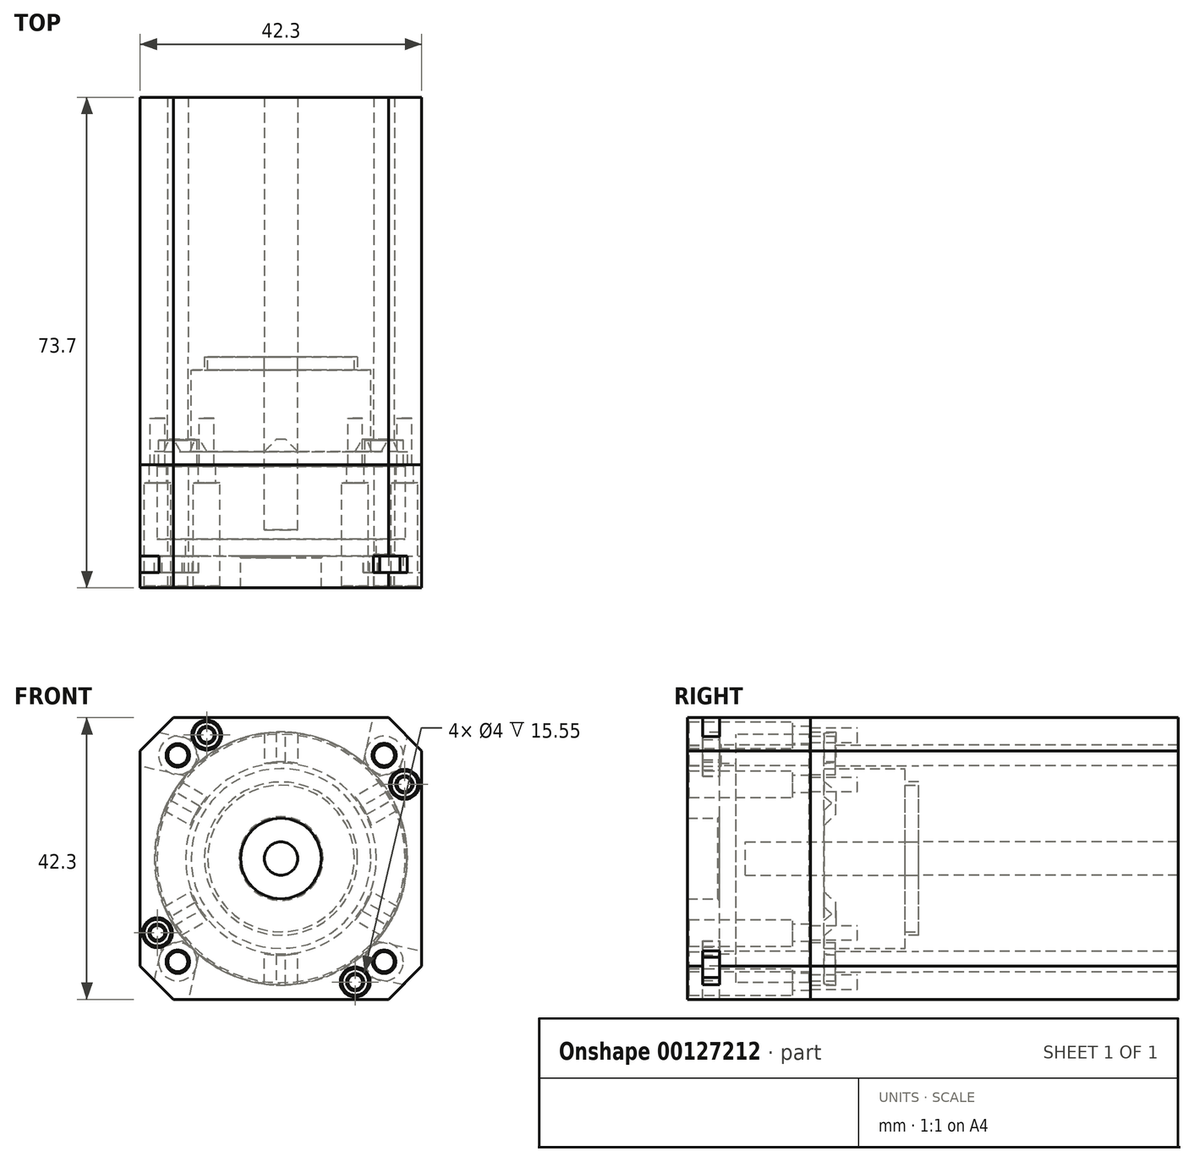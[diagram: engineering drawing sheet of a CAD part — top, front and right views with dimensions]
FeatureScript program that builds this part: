
annotation { "Feature Type Name" : "Feature", "Feature Type Description" : "" }
export const myFeature = defineFeature(function(context is Context, id is Id, definition is map)
    precondition{}
    {
        {
            var Q0;
            Q0=qCreatedBy(makeId("Front.planeOp"),FACE);
            var sketch = newSketch(context, id + "F0", { "sketchPlane" : qUnion([Q0])});
            skCircle(sketch, "E0", {"center": v(0, 0) * mm, "radius": 2.5 * mm});
            skLineSegment(sketch, "E1.bottom", {"start": v(21.15, -21.15) * mm, "end": v(-21.15, -21.15) * mm});
            skLineSegment(sketch, "E1.top", {"start": v(21.15, 21.15) * mm, "end": v(-21.15, 21.15) * mm});
            skLineSegment(sketch, "E1.left", {"start": v(21.15, -21.15) * mm, "end": v(21.15, 21.15) * mm});
            skLineSegment(sketch, "E1.right", {"start": v(-21.15, -21.15) * mm, "end": v(-21.15, 21.15) * mm});
            skCircle(sketch, "E2", {"center": v(0, 0) * mm, "radius": 11 * mm});
            skLineSegment(sketch, "E3", {"start": v(21.15, 21.15) * mm, "end": v(15.5, 21.15) * mm, "construction": true});
            skLineSegment(sketch, "E4", {"start": v(15.5, 21.15) * mm, "end": v(15.5, 15.5) * mm, "construction": true});
            skCircle(sketch, "E5", {"center": v(15.5, 15.5) * mm, "radius": 1.55 * mm});
            skCircle(sketch, "E6.1.0", {"center": v(-15.5, 15.5) * mm, "radius": 1.55 * mm});
            skCircle(sketch, "E6.2.0", {"center": v(-15.5, -15.5) * mm, "radius": 1.55 * mm});
            skCircle(sketch, "E6.3.0", {"center": v(15.5, -15.5) * mm, "radius": 1.55 * mm});
            skSolve(sketch);
        }
        {
            var Q0;
            Q0 = qSketchRegion(id + "F0", true);
            var Q1;
            Q1=makeQuery(id+"F0.imprint","IMPRINT",FACE,{"disambiguationData":[TD([[makeQuery(id+"F0.imprint","IMPRINT",EDGE,{"derivedFrom":sQuery(id+"F0.wireOp",EDGE,"E0")}),-1.0]])]});
            extrude(context, id + "F1", {"entities" : qUnion([Q0, Q1]), "oppositeDirection" : true, "depth" : 39 * mm});
        }
        {
            var Q0;
            Q0=makeQuery(id+"F0.imprint","IMPRINT",FACE,{"disambiguationData":[TD([[makeQuery(id+"F0.imprint","IMPRINT",EDGE,{"derivedFrom":sQuery(id+"F0.wireOp",EDGE,"E0")}),1.0]])]});
            extrude(context, id + "F2", {"entities" : qUnion([Q0]), "depth" : 26 * mm});
        }
        {
            var Q0;
            Q0=makeQuery(id+"F0.imprint","IMPRINT",FACE,{"disambiguationData":[TD([[makeQuery(id+"F0.imprint","IMPRINT",EDGE,{"derivedFrom":sQuery(id+"F0.wireOp",EDGE,"E0")}),-1.0]])]});
            extrude(context, id + "F3", {"entities" : qUnion([Q0]), "depth" : 2 * mm});
        }
        {
            var Q0;
            Q0=makeQuery(id+"F1.opExtrude","SWEPT_EDGE",EDGE,{"disambiguationData":[OSD([sQuery(id+"F0.wireOp",EDGE,"E1.top"),sQuery(id+"F0.wireOp",EDGE,"E1.left")])]});
            var Q1;
            Q1=makeQuery(id+"F1.opExtrude","SWEPT_EDGE",EDGE,{"disambiguationData":[OSD([sQuery(id+"F0.wireOp",EDGE,"E1.bottom"),sQuery(id+"F0.wireOp",EDGE,"E1.left")])]});
            var Q2;
            Q2=makeQuery(id+"F1.opExtrude","SWEPT_EDGE",EDGE,{"disambiguationData":[OSD([sQuery(id+"F0.wireOp",EDGE,"E1.bottom"),sQuery(id+"F0.wireOp",EDGE,"E1.right")])]});
            var Q3;
            Q3=makeQuery(id+"F1.opExtrude","SWEPT_EDGE",EDGE,{"disambiguationData":[OSD([sQuery(id+"F0.wireOp",EDGE,"E1.top"),sQuery(id+"F0.wireOp",EDGE,"E1.right")])]});
            chamfer(context, id + "F4", {"entities" : qUnion([Q0, Q1, Q2, Q3]), "width" : 5 * mm, "tangentPropagation" : true});
        }
        {
            var Q0;
            Q0=qCreatedBy(makeId("Front.planeOp"),FACE);
            cPlane(context, id + "F5", {"entities" : qUnion([Q0]), "cplaneType" : CPlaneType.OFFSET, "offset" : 2 * mm, "width" : 150 * mm, "height" : 150 * mm});
        }
        {
            var Q0;
            Q0=qCreatedBy(id+"F5.planeOp",FACE);
            var sketch = newSketch(context, id + "F6", { "sketchPlane" : qUnion([Q0])});
            skCircle(sketch, "E7", {"center": v(0, 0) * mm, "radius": 2.5 * mm});
            skLineSegment(sketch, "E8.bottom", {"start": v(21.15, -21.15) * mm, "end": v(-21.15, -21.15) * mm});
            skLineSegment(sketch, "E8.top", {"start": v(21.15, 21.15) * mm, "end": v(-21.15, 21.15) * mm});
            skLineSegment(sketch, "E8.left", {"start": v(21.15, -21.15) * mm, "end": v(21.15, 21.15) * mm});
            skLineSegment(sketch, "E8.right", {"start": v(-21.15, -21.15) * mm, "end": v(-21.15, 21.15) * mm});
            skCircle(sketch, "E9", {"center": v(0, 0) * mm, "radius": 11.5 * mm});
            skLineSegment(sketch, "E10", {"start": v(21.15, 21.15) * mm, "end": v(15.5, 21.15) * mm, "construction": true});
            skLineSegment(sketch, "E11", {"start": v(15.5, 21.15) * mm, "end": v(15.5, 15.5) * mm, "construction": true});
            skCircle(sketch, "E12", {"center": v(15.5, 15.5) * mm, "radius": 1.55 * mm});
            skCircle(sketch, "E13.1.0", {"center": v(-15.5, 15.5) * mm, "radius": 1.55 * mm});
            skCircle(sketch, "E13.2.0", {"center": v(-15.5, -15.5) * mm, "radius": 1.55 * mm});
            skCircle(sketch, "E13.3.0", {"center": v(15.5, -15.5) * mm, "radius": 1.55 * mm});
            skCircle(sketch, "E14", {"center": v(0, 0) * mm, "radius": 13.5 * mm});
            skSolve(sketch);
        }
        {
            var Q0;
            Q0=makeQuery(id+"F6.imprint","IMPRINT",FACE,{"disambiguationData":[TD([[makeQuery(id+"F6.imprint","IMPRINT",EDGE,{"derivedFrom":sQuery(id+"F6.wireOp",EDGE,"E8.bottom")}),-1.0]])]});
            extrude(context, id + "F7", {"entities" : qUnion([Q0]), "operationType" : NewBodyOperationType.ADD, "depth" : 12.2 * mm});
        }
        {
            var Q0;
            Q0=makeQuery(id+"F6.imprint","IMPRINT",FACE,{"disambiguationData":[TD([[makeQuery(id+"F6.imprint","IMPRINT",EDGE,{"derivedFrom":sQuery(id+"F6.wireOp",EDGE,"E9")}),-1.0]])]});
            var Q1;
            Q1=makeQuery(id+"F6.imprint","IMPRINT",FACE,{"disambiguationData":[TD([[makeQuery(id+"F6.imprint","IMPRINT",EDGE,{"derivedFrom":sQuery(id+"F6.wireOp",EDGE,"E8.bottom")}),-1.0]])]});
            extrude(context, id + "F8", {"entities" : qUnion([Q0, Q1]), "operationType" : NewBodyOperationType.ADD, "oppositeDirection" : true, "depth" : 2 * mm});
        }
        {
            var Q0;
            Q0=qCreatedBy(id+"F5.planeOp",FACE);
            cPlane(context, id + "F9", {"entities" : qUnion([Q0]), "cplaneType" : CPlaneType.OFFSET, "offset" : 12.2 * mm, "width" : 150 * mm, "height" : 150 * mm});
        }
        {
            var Q0;
            Q0=qCreatedBy(id+"F9.planeOp",FACE);
            var sketch = newSketch(context, id + "F10", { "sketchPlane" : qUnion([Q0])});
            skCircle(sketch, "E15", {"center": v(0, 0) * mm, "radius": 2.5 * mm});
            skLineSegment(sketch, "E16.bottom", {"start": v(21.15, -21.15) * mm, "end": v(-21.15, -21.15) * mm});
            skLineSegment(sketch, "E16.top", {"start": v(21.15, 21.15) * mm, "end": v(-21.15, 21.15) * mm});
            skLineSegment(sketch, "E16.left", {"start": v(21.15, -21.15) * mm, "end": v(21.15, 21.15) * mm});
            skLineSegment(sketch, "E16.right", {"start": v(-21.15, -21.15) * mm, "end": v(-21.15, 21.15) * mm});
            skCircle(sketch, "E17", {"center": v(0, 0) * mm, "radius": 11.5 * mm});
            skLineSegment(sketch, "E18", {"start": v(21.15, 21.15) * mm, "end": v(15.5, 21.15) * mm, "construction": true});
            skLineSegment(sketch, "E19", {"start": v(15.5, 21.15) * mm, "end": v(15.5, 15.5) * mm, "construction": true});
            skCircle(sketch, "E20", {"center": v(15.5, 15.5) * mm, "radius": 1.55 * mm});
            skCircle(sketch, "E21.1.0", {"center": v(-15.5, 15.5) * mm, "radius": 1.55 * mm});
            skCircle(sketch, "E21.2.0", {"center": v(-15.5, -15.5) * mm, "radius": 1.55 * mm});
            skCircle(sketch, "E21.3.0", {"center": v(15.5, -15.5) * mm, "radius": 1.55 * mm});
            skCircle(sketch, "E22", {"center": v(0, 0) * mm, "radius": 13.5 * mm});
            skCircle(sketch, "E23", {"center": v(0, 0) * mm, "radius": 19 * mm});
            skCircle(sketch, "E24", {"center": v(0, 0) * mm, "radius": 14.5 * mm});
            skLineSegment(sketch, "E25", {"start": v(2.5, 18.83) * mm, "end": v(2.5, 14.28) * mm});
            skLineSegment(sketch, "E26", {"start": v(-2.5, 18.83) * mm, "end": v(-2.5, 14.28) * mm});
            skCircle(sketch, "E27", {"center": v(18.55, 11.15) * mm, "radius": 1.1 * mm});
            skCircle(sketch, "E28.1.0", {"center": v(-11.15, 18.55) * mm, "radius": 1.1 * mm});
            skCircle(sketch, "E28.2.0", {"center": v(-18.55, -11.15) * mm, "radius": 1.1 * mm});
            skCircle(sketch, "E28.3.0", {"center": v(11.15, -18.55) * mm, "radius": 1.1 * mm});
            skCircle(sketch, "E29", {"center": v(-15.5, 15.5) * mm, "radius": 2.88 * mm});
            skCircle(sketch, "E30.1.0", {"center": v(-15.5, -15.5) * mm, "radius": 2.88 * mm});
            skCircle(sketch, "E30.2.0", {"center": v(15.5, -15.5) * mm, "radius": 2.88 * mm});
            skCircle(sketch, "E30.3.0", {"center": v(15.5, 15.5) * mm, "radius": 2.88 * mm});
            skLineSegment(sketch, "E31", {"start": v(0, 0) * mm, "end": v(0, 19) * mm, "construction": true});
            skLineSegment(sketch, "E32.1.0", {"start": v(-17.56, 7.25) * mm, "end": v(-13.62, 4.98) * mm});
            skLineSegment(sketch, "E32.1.1", {"start": v(-15.06, 11.58) * mm, "end": v(-11.12, 9.3) * mm});
            skLineSegment(sketch, "E32.2.0", {"start": v(-15.06, -11.58) * mm, "end": v(-11.12, -9.3) * mm});
            skLineSegment(sketch, "E32.2.1", {"start": v(-17.56, -7.25) * mm, "end": v(-13.62, -4.98) * mm});
            skLineSegment(sketch, "E32.3.0", {"start": v(2.5, -18.83) * mm, "end": v(2.5, -14.28) * mm});
            skLineSegment(sketch, "E32.3.1", {"start": v(-2.5, -18.83) * mm, "end": v(-2.5, -14.28) * mm});
            skLineSegment(sketch, "E32.4.0", {"start": v(17.56, -7.25) * mm, "end": v(13.62, -4.98) * mm});
            skLineSegment(sketch, "E32.4.1", {"start": v(15.06, -11.58) * mm, "end": v(11.12, -9.3) * mm});
            skLineSegment(sketch, "E32.5.0", {"start": v(15.06, 11.58) * mm, "end": v(11.12, 9.3) * mm});
            skLineSegment(sketch, "E32.5.1", {"start": v(17.56, 7.25) * mm, "end": v(13.62, 4.98) * mm});
            skSolve(sketch);
        }
        {
            var Q0;
            Q0=makeQuery(id+"F10.imprint","IMPRINT",FACE,{"disambiguationData":[TD([[makeQuery(id+"F10.imprint","IMPRINT",EDGE,{"derivedFrom":sQuery(id+"F10.wireOp",EDGE,"E16.bottom")}),-1.0]])]});
            extrude(context, id + "F11", {"entities" : qUnion([Q0]), "operationType" : NewBodyOperationType.ADD, "depth" : 2 * mm});
        }
        {
            var Q0;
            Q0=makeQuery(id+"F11.boolean.opBoolean","SPLIT",FACE,{"disambiguationData":[TD([makeQuery(id+"F11.opExtrude","SWEPT_FACE",FACE,{"disambiguationData":[OSD([sQuery(id+"F10.wireOp",EDGE,"E28.1.0")])]})])],"derivedFrom":makeQuery(id+"F7.opExtrude","CAP_FACE",FACE,{"disambiguationData":[OSD([sQuery(id+"F6.wireOp",EDGE,"E8.bottom"),sQuery(id+"F6.wireOp",EDGE,"E8.top"),sQuery(id+"F6.wireOp",EDGE,"E8.left"),sQuery(id+"F6.wireOp",EDGE,"E8.right"),sQuery(id+"F6.wireOp",EDGE,"E12"),sQuery(id+"F6.wireOp",EDGE,"E13.1.0"),sQuery(id+"F6.wireOp",EDGE,"E13.2.0"),sQuery(id+"F6.wireOp",EDGE,"E13.3.0"),sQuery(id+"F6.wireOp",EDGE,"E14")])],"isStart":false})});
            var Q1;
            Q1=makeQuery(id+"F11.boolean.opBoolean","SPLIT",FACE,{"disambiguationData":[TD([makeQuery(id+"F11.opExtrude","SWEPT_FACE",FACE,{"disambiguationData":[OSD([sQuery(id+"F10.wireOp",EDGE,"E27")])]})])],"derivedFrom":makeQuery(id+"F7.opExtrude","CAP_FACE",FACE,{"disambiguationData":[OSD([sQuery(id+"F6.wireOp",EDGE,"E8.bottom"),sQuery(id+"F6.wireOp",EDGE,"E8.top"),sQuery(id+"F6.wireOp",EDGE,"E8.left"),sQuery(id+"F6.wireOp",EDGE,"E8.right"),sQuery(id+"F6.wireOp",EDGE,"E12"),sQuery(id+"F6.wireOp",EDGE,"E13.1.0"),sQuery(id+"F6.wireOp",EDGE,"E13.2.0"),sQuery(id+"F6.wireOp",EDGE,"E13.3.0"),sQuery(id+"F6.wireOp",EDGE,"E14")])],"isStart":false})});
            var Q2;
            Q2=makeQuery(id+"F11.boolean.opBoolean","SPLIT",FACE,{"disambiguationData":[TD([makeQuery(id+"F11.opExtrude","SWEPT_FACE",FACE,{"disambiguationData":[OSD([sQuery(id+"F10.wireOp",EDGE,"E28.2.0")])]})])],"derivedFrom":makeQuery(id+"F7.opExtrude","CAP_FACE",FACE,{"disambiguationData":[OSD([sQuery(id+"F6.wireOp",EDGE,"E8.bottom"),sQuery(id+"F6.wireOp",EDGE,"E8.top"),sQuery(id+"F6.wireOp",EDGE,"E8.left"),sQuery(id+"F6.wireOp",EDGE,"E8.right"),sQuery(id+"F6.wireOp",EDGE,"E12"),sQuery(id+"F6.wireOp",EDGE,"E13.1.0"),sQuery(id+"F6.wireOp",EDGE,"E13.2.0"),sQuery(id+"F6.wireOp",EDGE,"E13.3.0"),sQuery(id+"F6.wireOp",EDGE,"E14")])],"isStart":false})});
            var Q3;
            Q3=makeQuery(id+"F11.boolean.opBoolean","SPLIT",FACE,{"disambiguationData":[TD([makeQuery(id+"F11.opExtrude","SWEPT_FACE",FACE,{"disambiguationData":[OSD([sQuery(id+"F10.wireOp",EDGE,"E28.3.0")])]})])],"derivedFrom":makeQuery(id+"F7.opExtrude","CAP_FACE",FACE,{"disambiguationData":[OSD([sQuery(id+"F6.wireOp",EDGE,"E8.bottom"),sQuery(id+"F6.wireOp",EDGE,"E8.top"),sQuery(id+"F6.wireOp",EDGE,"E8.left"),sQuery(id+"F6.wireOp",EDGE,"E8.right"),sQuery(id+"F6.wireOp",EDGE,"E12"),sQuery(id+"F6.wireOp",EDGE,"E13.1.0"),sQuery(id+"F6.wireOp",EDGE,"E13.2.0"),sQuery(id+"F6.wireOp",EDGE,"E13.3.0"),sQuery(id+"F6.wireOp",EDGE,"E14")])],"isStart":false})});
            extrude(context, id + "F12", {"entities" : qUnion([Q0, Q1, Q2, Q3]), "operationType" : NewBodyOperationType.REMOVE, "oppositeDirection" : true, "depth" : 5 * mm});
        }
        {
            var Q0;
            {var subQ0=sQuery(id+"F10.wireOp",EDGE,"E25");Q0=makeQuery(id+"F10.imprint","IMPRINT",FACE,{"disambiguationData":[TD([[makeQuery(id+"F10.imprint","IMPRINT",EDGE,{"derivedFrom":subQ0}),-1.0]])]});}
            var Q1;
            {var subQ0=sQuery(id+"F10.wireOp",EDGE,"E32.5.0");Q1=makeQuery(id+"F10.imprint","IMPRINT",FACE,{"disambiguationData":[TD([[makeQuery(id+"F10.imprint","IMPRINT",EDGE,{"derivedFrom":subQ0}),1.0]])]});}
            var Q2;
            {var subQ0=sQuery(id+"F10.wireOp",EDGE,"E32.4.0");Q2=makeQuery(id+"F10.imprint","IMPRINT",FACE,{"disambiguationData":[TD([[makeQuery(id+"F10.imprint","IMPRINT",EDGE,{"derivedFrom":subQ0}),1.0]])]});}
            var Q3;
            {var subQ0=sQuery(id+"F10.wireOp",EDGE,"E32.3.0");Q3=makeQuery(id+"F10.imprint","IMPRINT",FACE,{"disambiguationData":[TD([[makeQuery(id+"F10.imprint","IMPRINT",EDGE,{"derivedFrom":subQ0}),1.0]])]});}
            var Q4;
            {var subQ0=sQuery(id+"F10.wireOp",EDGE,"E32.2.0");Q4=makeQuery(id+"F10.imprint","IMPRINT",FACE,{"disambiguationData":[TD([[makeQuery(id+"F10.imprint","IMPRINT",EDGE,{"derivedFrom":subQ0}),1.0]])]});}
            var Q5;
            {var subQ0=sQuery(id+"F10.wireOp",EDGE,"E32.1.0");Q5=makeQuery(id+"F10.imprint","IMPRINT",FACE,{"disambiguationData":[TD([[makeQuery(id+"F10.imprint","IMPRINT",EDGE,{"derivedFrom":subQ0}),1.0]])]});}
            extrude(context, id + "F13", {"entities" : qUnion([Q0, Q1, Q2, Q3, Q4, Q5]), "operationType" : NewBodyOperationType.REMOVE, "oppositeDirection" : true, "depth" : 1.8 * mm});
        }
        {
            var Q0;
            {var subQ0=sQuery(id+"F6.wireOp",EDGE,"E13.1.0");Q0=makeQuery(id+"F11.boolean.opBoolean","SPLIT",FACE,{"disambiguationData":[TD([makeQuery(id+"F7.opExtrude","SWEPT_FACE",FACE,{"disambiguationData":[OSD([subQ0])]})])],"derivedFrom":makeQuery(id+"F7.opExtrude","CAP_FACE",FACE,{"disambiguationData":[OSD([sQuery(id+"F6.wireOp",EDGE,"E8.bottom"),sQuery(id+"F6.wireOp",EDGE,"E8.top"),sQuery(id+"F6.wireOp",EDGE,"E8.left"),sQuery(id+"F6.wireOp",EDGE,"E8.right"),sQuery(id+"F6.wireOp",EDGE,"E12"),subQ0,sQuery(id+"F6.wireOp",EDGE,"E13.2.0"),sQuery(id+"F6.wireOp",EDGE,"E13.3.0"),sQuery(id+"F6.wireOp",EDGE,"E14")])],"isStart":false})});}
            var Q1;
            {var subQ0=sQuery(id+"F6.wireOp",EDGE,"E13.2.0");Q1=makeQuery(id+"F11.boolean.opBoolean","SPLIT",FACE,{"disambiguationData":[TD([makeQuery(id+"F7.opExtrude","SWEPT_FACE",FACE,{"disambiguationData":[OSD([subQ0])]})])],"derivedFrom":makeQuery(id+"F7.opExtrude","CAP_FACE",FACE,{"disambiguationData":[OSD([sQuery(id+"F6.wireOp",EDGE,"E8.bottom"),sQuery(id+"F6.wireOp",EDGE,"E8.top"),sQuery(id+"F6.wireOp",EDGE,"E8.left"),sQuery(id+"F6.wireOp",EDGE,"E8.right"),sQuery(id+"F6.wireOp",EDGE,"E12"),sQuery(id+"F6.wireOp",EDGE,"E13.1.0"),subQ0,sQuery(id+"F6.wireOp",EDGE,"E13.3.0"),sQuery(id+"F6.wireOp",EDGE,"E14")])],"isStart":false})});}
            var Q2;
            {var subQ0=sQuery(id+"F6.wireOp",EDGE,"E13.3.0");Q2=makeQuery(id+"F11.boolean.opBoolean","SPLIT",FACE,{"disambiguationData":[TD([makeQuery(id+"F7.opExtrude","SWEPT_FACE",FACE,{"disambiguationData":[OSD([subQ0])]})])],"derivedFrom":makeQuery(id+"F7.opExtrude","CAP_FACE",FACE,{"disambiguationData":[OSD([sQuery(id+"F6.wireOp",EDGE,"E8.bottom"),sQuery(id+"F6.wireOp",EDGE,"E8.top"),sQuery(id+"F6.wireOp",EDGE,"E8.left"),sQuery(id+"F6.wireOp",EDGE,"E8.right"),sQuery(id+"F6.wireOp",EDGE,"E12"),sQuery(id+"F6.wireOp",EDGE,"E13.1.0"),sQuery(id+"F6.wireOp",EDGE,"E13.2.0"),subQ0,sQuery(id+"F6.wireOp",EDGE,"E14")])],"isStart":false})});}
            var Q3;
            {var subQ0=sQuery(id+"F6.wireOp",EDGE,"E12");Q3=makeQuery(id+"F11.boolean.opBoolean","SPLIT",FACE,{"disambiguationData":[TD([makeQuery(id+"F7.opExtrude","SWEPT_FACE",FACE,{"disambiguationData":[OSD([subQ0])]})])],"derivedFrom":makeQuery(id+"F7.opExtrude","CAP_FACE",FACE,{"disambiguationData":[OSD([sQuery(id+"F6.wireOp",EDGE,"E8.bottom"),sQuery(id+"F6.wireOp",EDGE,"E8.top"),sQuery(id+"F6.wireOp",EDGE,"E8.left"),sQuery(id+"F6.wireOp",EDGE,"E8.right"),subQ0,sQuery(id+"F6.wireOp",EDGE,"E13.1.0"),sQuery(id+"F6.wireOp",EDGE,"E13.2.0"),sQuery(id+"F6.wireOp",EDGE,"E13.3.0"),sQuery(id+"F6.wireOp",EDGE,"E14")])],"isStart":false})});}
            extrude(context, id + "F14", {"entities" : qUnion([Q0, Q1, Q2, Q3]), "operationType" : NewBodyOperationType.REMOVE, "oppositeDirection" : true, "depth" : 1.7 * mm});
        }
        {
            var Q0;
            Q0=makeQuery(id+"F13.boolean.opBoolean","COPY",EDGE,{"derivedFrom":makeQuery(id+"F13.opExtrude","CAP_EDGE",EDGE,{"disambiguationData":[OSD([sQuery(id+"F10.wireOp",EDGE,"E26")])],"isStart":false})});
            var Q1;
            Q1=makeQuery(id+"F13.boolean.opBoolean","COPY",EDGE,{"derivedFrom":makeQuery(id+"F13.opExtrude","CAP_EDGE",EDGE,{"disambiguationData":[OSD([sQuery(id+"F10.wireOp",EDGE,"E32.1.1")])],"isStart":false})});
            var Q2;
            Q2=makeQuery(id+"F13.boolean.opBoolean","COPY",EDGE,{"derivedFrom":makeQuery(id+"F13.opExtrude","CAP_EDGE",EDGE,{"disambiguationData":[OSD([sQuery(id+"F10.wireOp",EDGE,"E32.5.0")])],"isStart":false})});
            var Q3;
            Q3=makeQuery(id+"F13.boolean.opBoolean","COPY",EDGE,{"derivedFrom":makeQuery(id+"F13.opExtrude","CAP_EDGE",EDGE,{"disambiguationData":[OSD([sQuery(id+"F10.wireOp",EDGE,"E32.2.1")])],"isStart":false})});
            var Q4;
            Q4=makeQuery(id+"F13.boolean.opBoolean","COPY",EDGE,{"derivedFrom":makeQuery(id+"F13.opExtrude","CAP_EDGE",EDGE,{"disambiguationData":[OSD([sQuery(id+"F10.wireOp",EDGE,"E32.3.1")])],"isStart":false})});
            var Q5;
            Q5=makeQuery(id+"F13.boolean.opBoolean","COPY",EDGE,{"derivedFrom":makeQuery(id+"F13.opExtrude","CAP_EDGE",EDGE,{"disambiguationData":[OSD([sQuery(id+"F10.wireOp",EDGE,"E32.4.0")])],"isStart":false})});
            var Q6;
            Q6=makeQuery(id+"F13.boolean.opBoolean","COPY",EDGE,{"derivedFrom":makeQuery(id+"F13.opExtrude","CAP_EDGE",EDGE,{"disambiguationData":[OSD([sQuery(id+"F10.wireOp",EDGE,"E25")])],"isStart":false})});
            var Q7;
            Q7=makeQuery(id+"F13.boolean.opBoolean","COPY",EDGE,{"derivedFrom":makeQuery(id+"F13.opExtrude","CAP_EDGE",EDGE,{"disambiguationData":[OSD([sQuery(id+"F10.wireOp",EDGE,"E32.5.1")])],"isStart":false})});
            var Q8;
            Q8=makeQuery(id+"F13.boolean.opBoolean","COPY",EDGE,{"derivedFrom":makeQuery(id+"F13.opExtrude","CAP_EDGE",EDGE,{"disambiguationData":[OSD([sQuery(id+"F10.wireOp",EDGE,"E32.3.0")])],"isStart":false})});
            var Q9;
            Q9=makeQuery(id+"F13.boolean.opBoolean","COPY",EDGE,{"derivedFrom":makeQuery(id+"F13.opExtrude","CAP_EDGE",EDGE,{"disambiguationData":[OSD([sQuery(id+"F10.wireOp",EDGE,"E32.2.0")])],"isStart":false})});
            var Q10;
            Q10=makeQuery(id+"F13.boolean.opBoolean","COPY",EDGE,{"derivedFrom":makeQuery(id+"F13.opExtrude","CAP_EDGE",EDGE,{"disambiguationData":[OSD([sQuery(id+"F10.wireOp",EDGE,"E32.1.0")])],"isStart":false})});
            var Q11;
            Q11=makeQuery(id+"F13.boolean.opBoolean","COPY",EDGE,{"derivedFrom":makeQuery(id+"F13.opExtrude","CAP_EDGE",EDGE,{"disambiguationData":[OSD([sQuery(id+"F10.wireOp",EDGE,"E32.4.1")])],"isStart":false})});
            chamfer(context, id + "F15", {"entities" : qUnion([Q0, Q1, Q2, Q3, Q4, Q5, Q6, Q7, Q8, Q9, Q10, Q11]), "width" : 1.8 * mm, "tangentPropagation" : true});
        }
        {
            var Q0;
            Q0=qCreatedBy(id+"F9.planeOp",FACE);
            cPlane(context, id + "F16", {"entities" : qUnion([Q0]), "cplaneType" : CPlaneType.OFFSET, "offset" : 13.2 * mm, "width" : 150 * mm, "height" : 150 * mm});
        }
        {
            var Q0;
            Q0=qCreatedBy(id+"F16.planeOp",FACE);
            var sketch = newSketch(context, id + "F17", { "sketchPlane" : qUnion([Q0])});
            skLineSegment(sketch, "E33.bottom", {"start": v(21.15, -21.15) * mm, "end": v(-21.15, -21.15) * mm});
            skLineSegment(sketch, "E33.top", {"start": v(21.15, 21.15) * mm, "end": v(-21.15, 21.15) * mm});
            skLineSegment(sketch, "E33.left", {"start": v(21.15, -21.15) * mm, "end": v(21.15, 21.15) * mm});
            skLineSegment(sketch, "E33.right", {"start": v(-21.15, -21.15) * mm, "end": v(-21.15, 21.15) * mm});
            skPoint(sketch, "E33.middle", {"position": v(0, 0) * mm});
            skLineSegment(sketch, "E34", {"start": v(21.15, 21.15) * mm, "end": v(15.5, 21.15) * mm, "construction": true});
            skLineSegment(sketch, "E35", {"start": v(15.5, 21.15) * mm, "end": v(15.5, 15.5) * mm, "construction": true});
            skCircle(sketch, "E36", {"center": v(15.5, 15.5) * mm, "radius": 1.55 * mm});
            skCircle(sketch, "E37.1.0", {"center": v(-15.5, 15.5) * mm, "radius": 1.55 * mm});
            skCircle(sketch, "E37.2.0", {"center": v(-15.5, -15.5) * mm, "radius": 1.55 * mm});
            skCircle(sketch, "E37.3.0", {"center": v(15.5, -15.5) * mm, "radius": 1.55 * mm});
            skCircle(sketch, "E38", {"center": v(0, 0) * mm, "radius": 18.65 * mm});
            skPoint(sketch, "E39.center", {"position": v(-0.77, 0.3) * mm});
            skLineSegment(sketch, "E39.anchor1", {"start": v(-0.77, 0.3) * mm, "end": v(-2.75, 12.92) * mm, "construction": true});
            skLineSegment(sketch, "E39.anchor2", {"start": v(-0.77, 0.3) * mm, "end": v(-13.7, 5.28) * mm, "construction": true});
            skCircle(sketch, "E40", {"center": v(0, 0) * mm, "radius": 6.2 * mm});
            skCircle(sketch, "E41", {"center": v(0, 0) * mm, "radius": 14.32 * mm});
            skSolve(sketch);
        }
        {
            var Q0;
            Q0=makeQuery(id+"F17.imprint","IMPRINT",FACE,{"disambiguationData":[TD([[makeQuery(id+"F17.imprint","IMPRINT",EDGE,{"derivedFrom":sQuery(id+"F17.wireOp",EDGE,"E33.bottom")}),-1.0]])]});
            extrude(context, id + "F18", {"entities" : qUnion([Q0]), "oppositeDirection" : true, "depth" : 11.2 * mm});
        }
        {
            var Q0;
            Q0=makeQuery(id+"F17.imprint","IMPRINT",FACE,{"disambiguationData":[TD([[makeQuery(id+"F17.imprint","IMPRINT",EDGE,{"derivedFrom":sQuery(id+"F17.wireOp",EDGE,"E33.bottom")}),-1.0]])]});
            var Q1;
            Q1=makeQuery(id+"F17.imprint","IMPRINT",FACE,{"disambiguationData":[TD([[makeQuery(id+"F17.imprint","IMPRINT",EDGE,{"derivedFrom":sQuery(id+"F17.wireOp",EDGE,"E38")}),1.0]])]});
            extrude(context, id + "F19", {"entities" : qUnion([Q0, Q1]), "operationType" : NewBodyOperationType.ADD, "depth" : 2.5 * mm});
        }
        {
            var Q0;
            Q0=qCreatedBy(id+"F16.planeOp",FACE);
            cPlane(context, id + "F20", {"entities" : qUnion([Q0]), "cplaneType" : CPlaneType.OFFSET, "offset" : 2.5 * mm, "width" : 150 * mm, "height" : 150 * mm});
        }
        {
            var Q0;
            Q0=qCreatedBy(id+"F20.planeOp",FACE);
            var sketch = newSketch(context, id + "F21", { "sketchPlane" : qUnion([Q0])});
            skLineSegment(sketch, "E42.bottom", {"start": v(21.15, -21.15) * mm, "end": v(-21.15, -21.15) * mm});
            skLineSegment(sketch, "E42.top", {"start": v(21.15, 21.15) * mm, "end": v(-21.15, 21.15) * mm});
            skLineSegment(sketch, "E42.left", {"start": v(21.15, -21.15) * mm, "end": v(21.15, 21.15) * mm});
            skLineSegment(sketch, "E42.right", {"start": v(-21.15, -21.15) * mm, "end": v(-21.15, 21.15) * mm});
            skPoint(sketch, "E42.middle", {"position": v(0, 0) * mm});
            skLineSegment(sketch, "E43", {"start": v(21.15, 21.15) * mm, "end": v(15.5, 21.15) * mm, "construction": true});
            skLineSegment(sketch, "E44", {"start": v(15.5, 21.15) * mm, "end": v(15.5, 15.5) * mm, "construction": true});
            skCircle(sketch, "E45", {"center": v(15.5, 15.5) * mm, "radius": 1.55 * mm});
            skCircle(sketch, "E46.1.0", {"center": v(-15.5, 15.5) * mm, "radius": 1.5 * mm});
            skCircle(sketch, "E46.2.0", {"center": v(-15.5, -15.5) * mm, "radius": 1.5 * mm});
            skCircle(sketch, "E46.3.0", {"center": v(15.5, -15.5) * mm, "radius": 1.5 * mm});
            skCircle(sketch, "E47", {"center": v(0, 0) * mm, "radius": 18.55 * mm});
            skPoint(sketch, "E48.center", {"position": v(-0.34, -2.47) * mm});
            skLineSegment(sketch, "E48.anchor1", {"start": v(-0.34, -2.47) * mm, "end": v(-2.4, 10.7) * mm, "construction": true});
            skLineSegment(sketch, "E48.anchor2", {"start": v(-0.34, -2.47) * mm, "end": v(-14.8, 3.1) * mm, "construction": true});
            skCircle(sketch, "E49", {"center": v(0, 0) * mm, "radius": 6.05 * mm});
            skCircle(sketch, "E50", {"center": v(0, 0) * mm, "radius": 14.1 * mm});
            skPoint(sketch, "E51.endSnap0", {"position": v(18.32, 21.15) * mm});
            skLineSegment(sketch, "E52", {"start": v(21.15, 11.15) * mm, "end": v(18.55, 11.15) * mm, "construction": true});
            skCircle(sketch, "E53", {"center": v(18.55, 11.15) * mm, "radius": 2 * mm});
            skCircle(sketch, "E54.1.0", {"center": v(-11.15, 18.55) * mm, "radius": 2 * mm});
            skCircle(sketch, "E54.2.0", {"center": v(-18.55, -11.15) * mm, "radius": 2 * mm});
            skCircle(sketch, "E54.3.0", {"center": v(11.15, -18.55) * mm, "radius": 2 * mm});
            skCircle(sketch, "E55", {"center": v(18.55, 11.15) * mm, "radius": 1.3 * mm});
            skCircle(sketch, "E56.1.0", {"center": v(-11.15, 18.55) * mm, "radius": 1.3 * mm});
            skCircle(sketch, "E56.2.0", {"center": v(-18.55, -11.15) * mm, "radius": 1.3 * mm});
            skCircle(sketch, "E56.3.0", {"center": v(11.15, -18.55) * mm, "radius": 1.3 * mm});
            skLineSegment(sketch, "E57.0", {"start": v(14.81, 12.34) * mm, "end": v(12.42, 14.52) * mm});
            skLineSegment(sketch, "E57.1", {"start": v(12.42, 14.52) * mm, "end": v(13.1, 17.68) * mm});
            skLineSegment(sketch, "E57.4", {"start": v(18.58, 16.48) * mm, "end": v(17.9, 13.32) * mm});
            skLineSegment(sketch, "E57.5", {"start": v(17.9, 13.32) * mm, "end": v(14.81, 12.34) * mm});
            skPoint(sketch, "E57.0.midPoint", {"position": v(13.62, 13.43) * mm});
            skLineSegment(sketch, "E58", {"start": v(13.1, 17.68) * mm, "end": v(13.87, 21.15) * mm});
            skLineSegment(sketch, "E59", {"start": v(18.58, 16.48) * mm, "end": v(19.6, 21.15) * mm});
            skLineSegment(sketch, "E60.1.0", {"start": v(-17.68, 13.1) * mm, "end": v(-21.15, 13.87) * mm});
            skLineSegment(sketch, "E60.1.1", {"start": v(-14.52, 12.42) * mm, "end": v(-17.68, 13.1) * mm});
            skLineSegment(sketch, "E60.1.2", {"start": v(-12.34, 14.81) * mm, "end": v(-14.52, 12.42) * mm});
            skLineSegment(sketch, "E60.1.3", {"start": v(-13.32, 17.9) * mm, "end": v(-12.34, 14.81) * mm});
            skLineSegment(sketch, "E60.1.4", {"start": v(-16.48, 18.58) * mm, "end": v(-13.32, 17.9) * mm});
            skLineSegment(sketch, "E60.1.5", {"start": v(-16.48, 18.58) * mm, "end": v(-21.15, 19.6) * mm});
            skLineSegment(sketch, "E60.2.0", {"start": v(-13.1, -17.68) * mm, "end": v(-13.87, -21.15) * mm});
            skLineSegment(sketch, "E60.2.1", {"start": v(-12.42, -14.52) * mm, "end": v(-13.1, -17.68) * mm});
            skLineSegment(sketch, "E60.2.2", {"start": v(-14.81, -12.34) * mm, "end": v(-12.42, -14.52) * mm});
            skLineSegment(sketch, "E60.2.3", {"start": v(-17.9, -13.32) * mm, "end": v(-14.81, -12.34) * mm});
            skLineSegment(sketch, "E60.2.4", {"start": v(-18.58, -16.48) * mm, "end": v(-17.9, -13.32) * mm});
            skLineSegment(sketch, "E60.2.5", {"start": v(-18.58, -16.48) * mm, "end": v(-19.6, -21.15) * mm});
            skLineSegment(sketch, "E60.3.0", {"start": v(17.68, -13.1) * mm, "end": v(21.15, -13.87) * mm});
            skLineSegment(sketch, "E60.3.1", {"start": v(14.52, -12.42) * mm, "end": v(17.68, -13.1) * mm});
            skLineSegment(sketch, "E60.3.2", {"start": v(12.34, -14.81) * mm, "end": v(14.52, -12.42) * mm});
            skLineSegment(sketch, "E60.3.3", {"start": v(13.32, -17.9) * mm, "end": v(12.34, -14.81) * mm});
            skLineSegment(sketch, "E60.3.4", {"start": v(16.48, -18.58) * mm, "end": v(13.32, -17.9) * mm});
            skLineSegment(sketch, "E60.3.5", {"start": v(16.48, -18.58) * mm, "end": v(21.15, -19.6) * mm});
            skLineSegment(sketch, "E61", {"start": v(-21.15, 13.87) * mm, "end": v(-21.15, 19.6) * mm});
            skLineSegment(sketch, "E62", {"start": v(-19.6, -21.15) * mm, "end": v(-13.87, -21.15) * mm});
            skLineSegment(sketch, "E63", {"start": v(21.15, -19.6) * mm, "end": v(21.15, -13.87) * mm});
            skSolve(sketch);
        }
        {
            var Q0;
            Q0=makeQuery(id+"F21.imprint","IMPRINT",FACE,{"disambiguationData":[TD([[makeQuery(id+"F21.imprint","IMPRINT",EDGE,{"derivedFrom":sQuery(id+"F21.wireOp",EDGE,"E49")}),-1.0]])]});
            var Q1;
            Q1=makeQuery(id+"F21.imprint","IMPRINT",FACE,{"disambiguationData":[TD([[makeQuery(id+"F21.imprint","IMPRINT",EDGE,{"derivedFrom":sQuery(id+"F21.wireOp",EDGE,"E47")}),1.0]])]});
            var Q2;
            Q2=makeQuery(id+"F21.imprint","IMPRINT",FACE,{"disambiguationData":[TD([[makeQuery(id+"F21.imprint","IMPRINT",EDGE,{"derivedFrom":sQuery(id+"F21.wireOp",EDGE,"E42.bottom")}),-1.0]])]});
            var Q3;
            Q3=makeQuery(id+"F21.imprint","IMPRINT",FACE,{"disambiguationData":[TD([[makeQuery(id+"F21.imprint","IMPRINT",EDGE,{"derivedFrom":sQuery(id+"F21.wireOp",EDGE,"E45")}),-1.0]])]});
            var Q4;
            Q4=makeQuery(id+"F21.imprint","IMPRINT",FACE,{"disambiguationData":[TD([[makeQuery(id+"F21.imprint","IMPRINT",EDGE,{"derivedFrom":sQuery(id+"F21.wireOp",EDGE,"E46.1.0")}),-1.0]])]});
            var Q5;
            Q5=makeQuery(id+"F21.imprint","IMPRINT",FACE,{"disambiguationData":[TD([[makeQuery(id+"F21.imprint","IMPRINT",EDGE,{"derivedFrom":sQuery(id+"F21.wireOp",EDGE,"E46.2.0")}),-1.0]])]});
            var Q6;
            Q6=makeQuery(id+"F21.imprint","IMPRINT",FACE,{"disambiguationData":[TD([[makeQuery(id+"F21.imprint","IMPRINT",EDGE,{"derivedFrom":sQuery(id+"F21.wireOp",EDGE,"E46.3.0")}),-1.0]])]});
            extrude(context, id + "F22", {"entities" : qUnion([Q0, Q1, Q2, Q3, Q4, Q5, Q6]), "operationType" : NewBodyOperationType.ADD, "depth" : 4.8 * mm});
        }
        {
            var Q0;
            Q0=makeQuery(id+"F21.imprint","IMPRINT",FACE,{"disambiguationData":[TD([[makeQuery(id+"F21.imprint","IMPRINT",EDGE,{"derivedFrom":sQuery(id+"F21.wireOp",EDGE,"E56.1.0")}),1.0]])]});
            var Q1;
            Q1=makeQuery(id+"F21.imprint","IMPRINT",FACE,{"disambiguationData":[TD([[makeQuery(id+"F21.imprint","IMPRINT",EDGE,{"derivedFrom":sQuery(id+"F21.wireOp",EDGE,"E55")}),1.0]])]});
            var Q2;
            Q2=makeQuery(id+"F21.imprint","IMPRINT",FACE,{"disambiguationData":[TD([[makeQuery(id+"F21.imprint","IMPRINT",EDGE,{"derivedFrom":sQuery(id+"F21.wireOp",EDGE,"E56.2.0")}),1.0]])]});
            var Q3;
            Q3=makeQuery(id+"F21.imprint","IMPRINT",FACE,{"disambiguationData":[TD([[makeQuery(id+"F21.imprint","IMPRINT",EDGE,{"derivedFrom":sQuery(id+"F21.wireOp",EDGE,"E56.3.0")}),1.0]])]});
            var Q4;
            Q4=makeQuery(id+"F18.opExtrude","CAP_FACE",FACE,{"disambiguationData":[OSD([sQuery(id+"F17.wireOp",EDGE,"E33.bottom"),sQuery(id+"F17.wireOp",EDGE,"E33.top"),sQuery(id+"F17.wireOp",EDGE,"E33.left"),sQuery(id+"F17.wireOp",EDGE,"E33.right"),sQuery(id+"F17.wireOp",EDGE,"E36"),sQuery(id+"F17.wireOp",EDGE,"E37.1.0"),sQuery(id+"F17.wireOp",EDGE,"E37.2.0"),sQuery(id+"F17.wireOp",EDGE,"E37.3.0"),sQuery(id+"F17.wireOp",EDGE,"E38")])],"isStart":false});
            extrude(context, id + "F23", {"entities" : qUnion([Q0, Q1, Q2, Q3]), "operationType" : NewBodyOperationType.REMOVE, "endBound" : BoundingType.UP_TO_SURFACE, "oppositeDirection" : true, "endBoundEntityFace" : qUnion([Q4]), "depth" : 25 * mm});
        }
        {
            var Q0;
            Q0=makeQuery(id+"F21.imprint","IMPRINT",FACE,{"disambiguationData":[TD([[makeQuery(id+"F21.imprint","IMPRINT",EDGE,{"derivedFrom":sQuery(id+"F21.wireOp",EDGE,"E46.3.0")}),-1.0]])]});
            var Q1;
            Q1=makeQuery(id+"F21.imprint","IMPRINT",FACE,{"disambiguationData":[TD([[makeQuery(id+"F21.imprint","IMPRINT",EDGE,{"derivedFrom":sQuery(id+"F21.wireOp",EDGE,"E46.2.0")}),-1.0]])]});
            var Q2;
            Q2=makeQuery(id+"F21.imprint","IMPRINT",FACE,{"disambiguationData":[TD([[makeQuery(id+"F21.imprint","IMPRINT",EDGE,{"derivedFrom":sQuery(id+"F21.wireOp",EDGE,"E46.1.0")}),-1.0]])]});
            var Q3;
            Q3=makeQuery(id+"F21.imprint","IMPRINT",FACE,{"disambiguationData":[TD([[makeQuery(id+"F21.imprint","IMPRINT",EDGE,{"derivedFrom":sQuery(id+"F21.wireOp",EDGE,"E45")}),-1.0]])]});
            extrude(context, id + "F24", {"entities" : qUnion([Q0, Q1, Q2, Q3]), "operationType" : NewBodyOperationType.REMOVE, "depth" : 2.5 * mm});
        }
        {
            var Q0;
            Q0=makeQuery(id+"F21.imprint","IMPRINT",FACE,{"disambiguationData":[TD([[makeQuery(id+"F21.imprint","IMPRINT",EDGE,{"derivedFrom":sQuery(id+"F21.wireOp",EDGE,"E54.3.0")}),1.0]])]});
            var Q1;
            Q1=makeQuery(id+"F21.imprint","IMPRINT",FACE,{"disambiguationData":[TD([[makeQuery(id+"F21.imprint","IMPRINT",EDGE,{"derivedFrom":sQuery(id+"F21.wireOp",EDGE,"E54.2.0")}),1.0]])]});
            var Q2;
            Q2=makeQuery(id+"F21.imprint","IMPRINT",FACE,{"disambiguationData":[TD([[makeQuery(id+"F21.imprint","IMPRINT",EDGE,{"derivedFrom":sQuery(id+"F21.wireOp",EDGE,"E54.1.0")}),1.0]])]});
            var Q3;
            Q3=makeQuery(id+"F21.imprint","IMPRINT",FACE,{"disambiguationData":[TD([[makeQuery(id+"F21.imprint","IMPRINT",EDGE,{"derivedFrom":sQuery(id+"F21.wireOp",EDGE,"E53")}),1.0]])]});
            extrude(context, id + "F25", {"entities" : qUnion([Q0, Q1, Q2, Q3]), "operationType" : NewBodyOperationType.REMOVE, "oppositeDirection" : true, "depth" : 11 * mm});
        }
        {
            var Q0;
            {var subQ0=sQuery(id+"F6.wireOp",EDGE,"E8.left");var subQ1=sQuery(id+"F6.wireOp",EDGE,"E8.top");Q0=makeQuery(id+"F8.boolean.opBoolean","MERGE",EDGE,{"derivedFrom":[makeQuery(id+"F7.opExtrude","SWEPT_EDGE",EDGE,{"disambiguationData":[OSD([subQ1,subQ0])]}),makeQuery(id+"F8.opExtrude","SWEPT_EDGE",EDGE,{"disambiguationData":[OSD([subQ1,subQ0])]})]});}
            var Q1;
            Q1=makeQuery(id+"F11.opExtrude","SWEPT_EDGE",EDGE,{"disambiguationData":[OSD([sQuery(id+"F10.wireOp",EDGE,"E16.top"),sQuery(id+"F10.wireOp",EDGE,"E16.left")])]});
            var Q2;
            {var subQ0=sQuery(id+"F17.wireOp",EDGE,"E33.left");var subQ1=sQuery(id+"F17.wireOp",EDGE,"E33.top");Q2=makeQuery(id+"F19.boolean.opBoolean","MERGE",EDGE,{"derivedFrom":[makeQuery(id+"F18.opExtrude","SWEPT_EDGE",EDGE,{"disambiguationData":[OSD([subQ1,subQ0])]}),makeQuery(id+"F19.opExtrude","SWEPT_EDGE",EDGE,{"disambiguationData":[OSD([subQ1,subQ0])]})]});}
            var Q3;
            {var subQ0=sQuery(id+"F6.wireOp",EDGE,"E8.right");var subQ1=sQuery(id+"F6.wireOp",EDGE,"E8.top");Q3=makeQuery(id+"F8.boolean.opBoolean","MERGE",EDGE,{"derivedFrom":[makeQuery(id+"F7.opExtrude","SWEPT_EDGE",EDGE,{"disambiguationData":[OSD([subQ1,subQ0])]}),makeQuery(id+"F8.opExtrude","SWEPT_EDGE",EDGE,{"disambiguationData":[OSD([subQ1,subQ0])]})]});}
            var Q4;
            {var subQ0=sQuery(id+"F17.wireOp",EDGE,"E33.right");var subQ1=sQuery(id+"F17.wireOp",EDGE,"E33.top");Q4=makeQuery(id+"F19.boolean.opBoolean","MERGE",EDGE,{"derivedFrom":[makeQuery(id+"F18.opExtrude","SWEPT_EDGE",EDGE,{"disambiguationData":[OSD([subQ1,subQ0])]}),makeQuery(id+"F19.opExtrude","SWEPT_EDGE",EDGE,{"disambiguationData":[OSD([subQ1,subQ0])]})]});}
            var Q5;
            Q5=makeQuery(id+"F11.opExtrude","SWEPT_EDGE",EDGE,{"disambiguationData":[OSD([sQuery(id+"F10.wireOp",EDGE,"E16.top"),sQuery(id+"F10.wireOp",EDGE,"E16.right")])]});
            var Q6;
            {var subQ0=sQuery(id+"F6.wireOp",EDGE,"E8.left");var subQ1=sQuery(id+"F6.wireOp",EDGE,"E8.bottom");Q6=makeQuery(id+"F8.boolean.opBoolean","MERGE",EDGE,{"derivedFrom":[makeQuery(id+"F7.opExtrude","SWEPT_EDGE",EDGE,{"disambiguationData":[OSD([subQ1,subQ0])]}),makeQuery(id+"F8.opExtrude","SWEPT_EDGE",EDGE,{"disambiguationData":[OSD([subQ1,subQ0])]})]});}
            var Q7;
            {var subQ0=sQuery(id+"F17.wireOp",EDGE,"E33.left");var subQ1=sQuery(id+"F17.wireOp",EDGE,"E33.bottom");Q7=makeQuery(id+"F19.boolean.opBoolean","MERGE",EDGE,{"derivedFrom":[makeQuery(id+"F18.opExtrude","SWEPT_EDGE",EDGE,{"disambiguationData":[OSD([subQ1,subQ0])]}),makeQuery(id+"F19.opExtrude","SWEPT_EDGE",EDGE,{"disambiguationData":[OSD([subQ1,subQ0])]})]});}
            var Q8;
            Q8=makeQuery(id+"F11.opExtrude","SWEPT_EDGE",EDGE,{"disambiguationData":[OSD([sQuery(id+"F10.wireOp",EDGE,"E16.bottom"),sQuery(id+"F10.wireOp",EDGE,"E16.left")])]});
            var Q9;
            {var subQ0=sQuery(id+"F6.wireOp",EDGE,"E8.right");var subQ1=sQuery(id+"F6.wireOp",EDGE,"E8.bottom");Q9=makeQuery(id+"F8.boolean.opBoolean","MERGE",EDGE,{"derivedFrom":[makeQuery(id+"F7.opExtrude","SWEPT_EDGE",EDGE,{"disambiguationData":[OSD([subQ1,subQ0])]}),makeQuery(id+"F8.opExtrude","SWEPT_EDGE",EDGE,{"disambiguationData":[OSD([subQ1,subQ0])]})]});}
            var Q10;
            {var subQ0=sQuery(id+"F17.wireOp",EDGE,"E33.right");var subQ1=sQuery(id+"F17.wireOp",EDGE,"E33.bottom");Q10=makeQuery(id+"F19.boolean.opBoolean","MERGE",EDGE,{"derivedFrom":[makeQuery(id+"F18.opExtrude","SWEPT_EDGE",EDGE,{"disambiguationData":[OSD([subQ1,subQ0])]}),makeQuery(id+"F19.opExtrude","SWEPT_EDGE",EDGE,{"disambiguationData":[OSD([subQ1,subQ0])]})]});}
            var Q11;
            Q11=makeQuery(id+"F11.opExtrude","SWEPT_EDGE",EDGE,{"disambiguationData":[OSD([sQuery(id+"F10.wireOp",EDGE,"E16.bottom"),sQuery(id+"F10.wireOp",EDGE,"E16.right")])]});
            var Q12;
            Q12=makeQuery(id+"F22.opExtrude","SWEPT_EDGE",EDGE,{"disambiguationData":[OSD([sQuery(id+"F21.wireOp",EDGE,"E42.bottom"),sQuery(id+"F21.wireOp",EDGE,"E42.right")])]});
            var Q13;
            Q13=makeQuery(id+"F22.opExtrude","SWEPT_EDGE",EDGE,{"disambiguationData":[OSD([sQuery(id+"F21.wireOp",EDGE,"E42.top"),sQuery(id+"F21.wireOp",EDGE,"E42.right")])]});
            var Q14;
            Q14=makeQuery(id+"F22.opExtrude","SWEPT_EDGE",EDGE,{"disambiguationData":[OSD([sQuery(id+"F21.wireOp",EDGE,"E42.top"),sQuery(id+"F21.wireOp",EDGE,"E42.left")])]});
            var Q15;
            Q15=makeQuery(id+"F22.opExtrude","SWEPT_EDGE",EDGE,{"disambiguationData":[OSD([sQuery(id+"F21.wireOp",EDGE,"E42.bottom"),sQuery(id+"F21.wireOp",EDGE,"E42.left")])]});
            chamfer(context, id + "F26", {"entities" : qUnion([Q0, Q1, Q2, Q3, Q4, Q5, Q6, Q7, Q8, Q9, Q10, Q11, Q12, Q13, Q14, Q15]), "width" : 5 * mm, "tangentPropagation" : true});
        }
        {
            var Q0;
            Q0=makeQuery(id+"F22.opExtrude","CAP_EDGE",EDGE,{"disambiguationData":[OSD([sQuery(id+"F21.wireOp",EDGE,"E54.1.0")])],"isStart":false});
            var Q1;
            Q1=makeQuery(id+"F22.opExtrude","CAP_EDGE",EDGE,{"disambiguationData":[OSD([sQuery(id+"F21.wireOp",EDGE,"E46.1.0")])],"isStart":false});
            var Q2;
            Q2=makeQuery(id+"F22.opExtrude","CAP_EDGE",EDGE,{"disambiguationData":[OSD([sQuery(id+"F21.wireOp",EDGE,"E45")])],"isStart":false});
            var Q3;
            Q3=makeQuery(id+"F22.opExtrude","CAP_EDGE",EDGE,{"disambiguationData":[OSD([sQuery(id+"F21.wireOp",EDGE,"E53")])],"isStart":false});
            var Q4;
            Q4=makeQuery(id+"F22.opExtrude","CAP_EDGE",EDGE,{"disambiguationData":[OSD([sQuery(id+"F21.wireOp",EDGE,"E54.2.0")])],"isStart":false});
            var Q5;
            Q5=makeQuery(id+"F22.opExtrude","CAP_EDGE",EDGE,{"disambiguationData":[OSD([sQuery(id+"F21.wireOp",EDGE,"E46.2.0")])],"isStart":false});
            var Q6;
            Q6=makeQuery(id+"F22.opExtrude","CAP_EDGE",EDGE,{"disambiguationData":[OSD([sQuery(id+"F21.wireOp",EDGE,"E54.3.0")])],"isStart":false});
            var Q7;
            Q7=makeQuery(id+"F22.opExtrude","CAP_EDGE",EDGE,{"disambiguationData":[OSD([sQuery(id+"F21.wireOp",EDGE,"E46.3.0")])],"isStart":false});
            var Q8;
            Q8=makeQuery(id+"F24.boolean.opBoolean","COPY",EDGE,{"derivedFrom":makeQuery(id+"F24.opExtrude","CAP_EDGE",EDGE,{"disambiguationData":[OSD([sQuery(id+"F21.wireOp",EDGE,"E46.2.0")])],"isStart":false})});
            var Q9;
            Q9=makeQuery(id+"F24.boolean.opBoolean","COPY",EDGE,{"derivedFrom":makeQuery(id+"F24.opExtrude","CAP_EDGE",EDGE,{"disambiguationData":[OSD([sQuery(id+"F21.wireOp",EDGE,"E46.3.0")])],"isStart":false})});
            var Q10;
            Q10=makeQuery(id+"F24.boolean.opBoolean","COPY",EDGE,{"derivedFrom":makeQuery(id+"F24.opExtrude","CAP_EDGE",EDGE,{"disambiguationData":[OSD([sQuery(id+"F21.wireOp",EDGE,"E45")])],"isStart":false})});
            var Q11;
            Q11=makeQuery(id+"F24.boolean.opBoolean","COPY",EDGE,{"derivedFrom":makeQuery(id+"F24.opExtrude","CAP_EDGE",EDGE,{"disambiguationData":[OSD([sQuery(id+"F21.wireOp",EDGE,"E46.1.0")])],"isStart":false})});
            var Q12;
            Q12=makeQuery(id+"F19.opExtrude","CAP_EDGE",EDGE,{"disambiguationData":[OSD([sQuery(id+"F17.wireOp",EDGE,"E37.1.0")])],"isStart":false});
            var Q13;
            {var subQ0=sQuery(id+"F21.wireOp",EDGE,"E45");Q13=makeQuery(id+"F24.boolean.opBoolean","MERGE",EDGE,{"derivedFrom":[makeQuery(id+"F22.boolean.opBoolean","MERGE",EDGE,{"derivedFrom":[makeQuery(id+"F19.opExtrude","CAP_EDGE",EDGE,{"disambiguationData":[OSD([sQuery(id+"F17.wireOp",EDGE,"E36")])],"isStart":false}),makeQuery(id+"F22.opExtrude","CAP_EDGE",EDGE,{"disambiguationData":[OSD([subQ0])],"isStart":true})]}),makeQuery(id+"F24.opExtrude","CAP_EDGE",EDGE,{"disambiguationData":[OSD([subQ0])],"isStart":true})]});}
            var Q14;
            Q14=makeQuery(id+"F19.opExtrude","CAP_EDGE",EDGE,{"disambiguationData":[OSD([sQuery(id+"F17.wireOp",EDGE,"E37.3.0")])],"isStart":false});
            var Q15;
            Q15=makeQuery(id+"F19.opExtrude","CAP_EDGE",EDGE,{"disambiguationData":[OSD([sQuery(id+"F17.wireOp",EDGE,"E37.2.0")])],"isStart":false});
            var Q16;
            Q16=makeQuery(id+"F22.opExtrude","CAP_EDGE",EDGE,{"disambiguationData":[OSD([sQuery(id+"F21.wireOp",EDGE,"E49")])],"isStart":true});
            var Q17;
            Q17=makeQuery(id+"F18.opExtrude","CAP_EDGE",EDGE,{"disambiguationData":[OSD([sQuery(id+"F17.wireOp",EDGE,"E38")])],"isStart":false});
            chamfer(context, id + "F27", {"entities" : qUnion([Q0, Q1, Q2, Q3, Q4, Q5, Q6, Q7, Q8, Q9, Q10, Q11, Q12, Q13, Q14, Q15, Q16, Q17]), "width" : 0.25 * mm, "tangentPropagation" : true});
        }
    });
